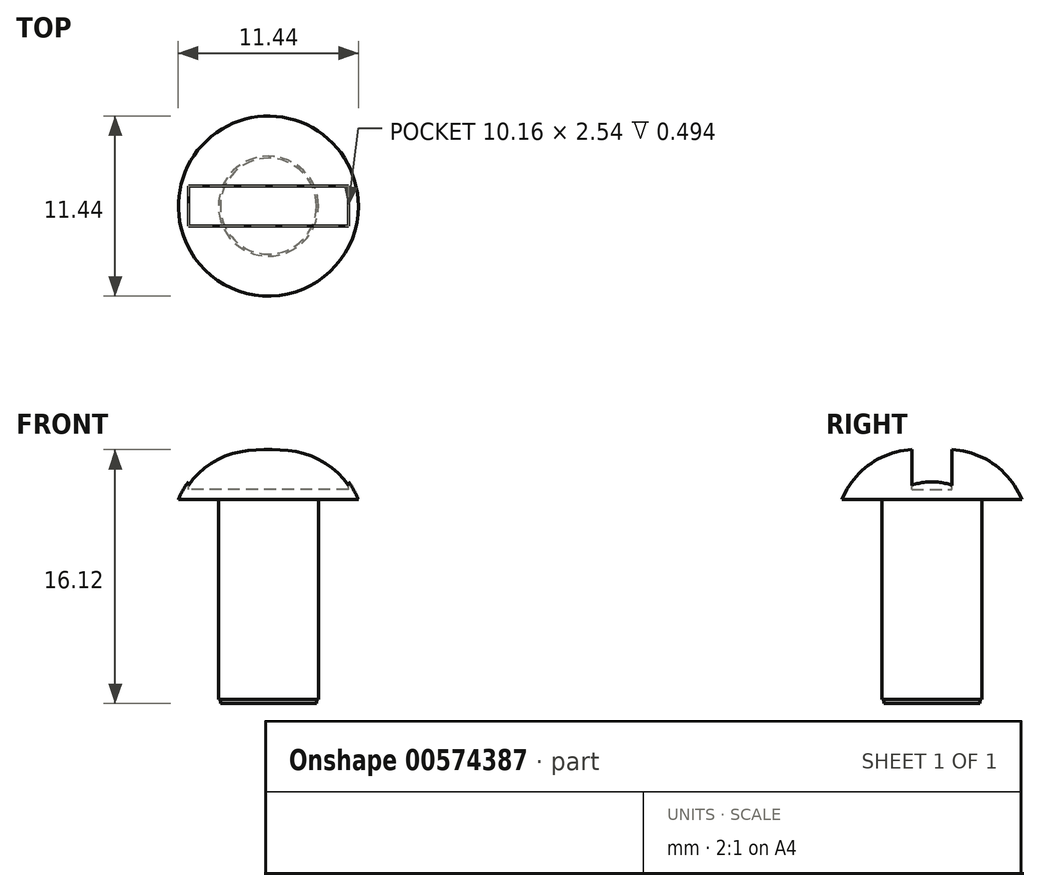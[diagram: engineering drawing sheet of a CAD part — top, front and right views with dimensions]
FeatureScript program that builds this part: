
annotation { "Feature Type Name" : "Feature", "Feature Type Description" : "" }
export const myFeature = defineFeature(function(context is Context, id is Id, definition is map)
    precondition{}
    {
        {
            var Q0;
            Q0=qCreatedBy(makeId("Top.planeOp"),FACE);
            var sketch = newSketch(context, id + "F0", { "sketchPlane" : qUnion([Q0])});
            skLineSegment(sketch, "E0", {"start": v(0, 6.96) * mm, "end": v(0, -6.36) * mm, "construction": true});
            skCircle(sketch, "E1", {"center": v(0, 0) * mm, "radius": 3.18 * mm});
            skSolve(sketch);
        }
        {
            var Q0;
            Q0=qCreatedBy(makeId("Top.planeOp"),FACE);
            cPlane(context, id + "F1", {"entities" : qUnion([Q0]), "cplaneType" : CPlaneType.OFFSET, "offset" : 12.7 * mm, "width" : 152.4 * mm, "height" : 152.4 * mm});
        }
        {
            var Q0;
            Q0=qCreatedBy(id+"F1.planeOp",FACE);
            var sketch = newSketch(context, id + "F2", { "sketchPlane" : qUnion([Q0])});
            skCircle(sketch, "E2", {"center": v(0, 0) * mm, "radius": 5.72 * mm});
            skSolve(sketch);
        }
        {
            var Q0;
            Q0=makeQuery(id+"F2.imprint","IMPRINT",FACE,{"disambiguationData":[TD([[makeQuery(id+"F2.imprint","IMPRINT",EDGE,{"derivedFrom":sQuery(id+"F2.wireOp",EDGE,"E2")}),1.0]])]});
            extrude(context, id + "F3", {"entities" : qUnion([Q0]), "depth" : 3.17 * mm, "offsetDistance" : 25.4 * mm});
        }
        {
            var Q0;
            Q0=makeQuery(id+"F3.opExtrude","CAP_EDGE",EDGE,{"disambiguationData":[OSD([sQuery(id+"F2.wireOp",EDGE,"E2")])],"isStart":false});
            fillet(context, id + "F4", {"entities" : qUnion([Q0]), "radius" : 5.08 * mm, "tangentPropagation" : true, "allowEdgeOverflow" : false});
        }
        {
            var Q0;
            Q0=makeQuery(id+"F3.opExtrude","CAP_FACE",FACE,{"disambiguationData":[OSD([sQuery(id+"F2.wireOp",EDGE,"E2")])],"isStart":false});
            var sketch = newSketch(context, id + "F5", { "sketchPlane" : qUnion([Q0])});
            skLineSegment(sketch, "E3.bottom", {"start": v(5.08, -1.27) * mm, "end": v(-5.08, -1.27) * mm});
            skLineSegment(sketch, "E3.top", {"start": v(5.08, 1.27) * mm, "end": v(-5.08, 1.27) * mm});
            skLineSegment(sketch, "E3.left", {"start": v(5.08, -1.27) * mm, "end": v(5.08, 1.27) * mm});
            skLineSegment(sketch, "E3.right", {"start": v(-5.08, -1.27) * mm, "end": v(-5.08, 1.27) * mm});
            skSolve(sketch);
        }
        {
            var Q0;
            Q0 = qSketchRegion(id + "F5", true);
            extrude(context, id + "F6", {"entities" : qUnion([Q0]), "operationType" : NewBodyOperationType.REMOVE, "oppositeDirection" : true, "depth" : 2.54 * mm, "offsetDistance" : 25.4 * mm});
        }
        {
            var Q0;
            Q0 = qSketchRegion(id + "F0", true);
            var Q1;
            Q1=sQuery(id+"F0.wireOp",EDGE,"E1");
            extrude(context, id + "F7", {"entities" : qUnion([Q0]), "surfaceEntities" : qUnion([Q1]), "depth" : 12.7 * mm, "offsetDistance" : 25.4 * mm});
        }
        {
            var Q0;
            Q0=makeQuery(id+"F7.opExtrude","CAP_FACE",FACE,{"disambiguationData":[OSD([sQuery(id+"F0.wireOp",EDGE,"E1")])],"isStart":true});
            var sketch = newSketch(context, id + "F8", { "sketchPlane" : qUnion([Q0])});
            skCircle(sketch, "E4", {"center": v(0, 0) * mm, "radius": 3.05 * mm});
            skSolve(sketch);
        }
        {
            var Q0;
            Q0 = qSketchRegion(id + "F8", true);
            extrude(context, id + "F9", {"entities" : qUnion([Q0]), "operationType" : NewBodyOperationType.ADD, "depth" : 0.25 * mm, "offsetDistance" : 25.4 * mm});
        }
    });
